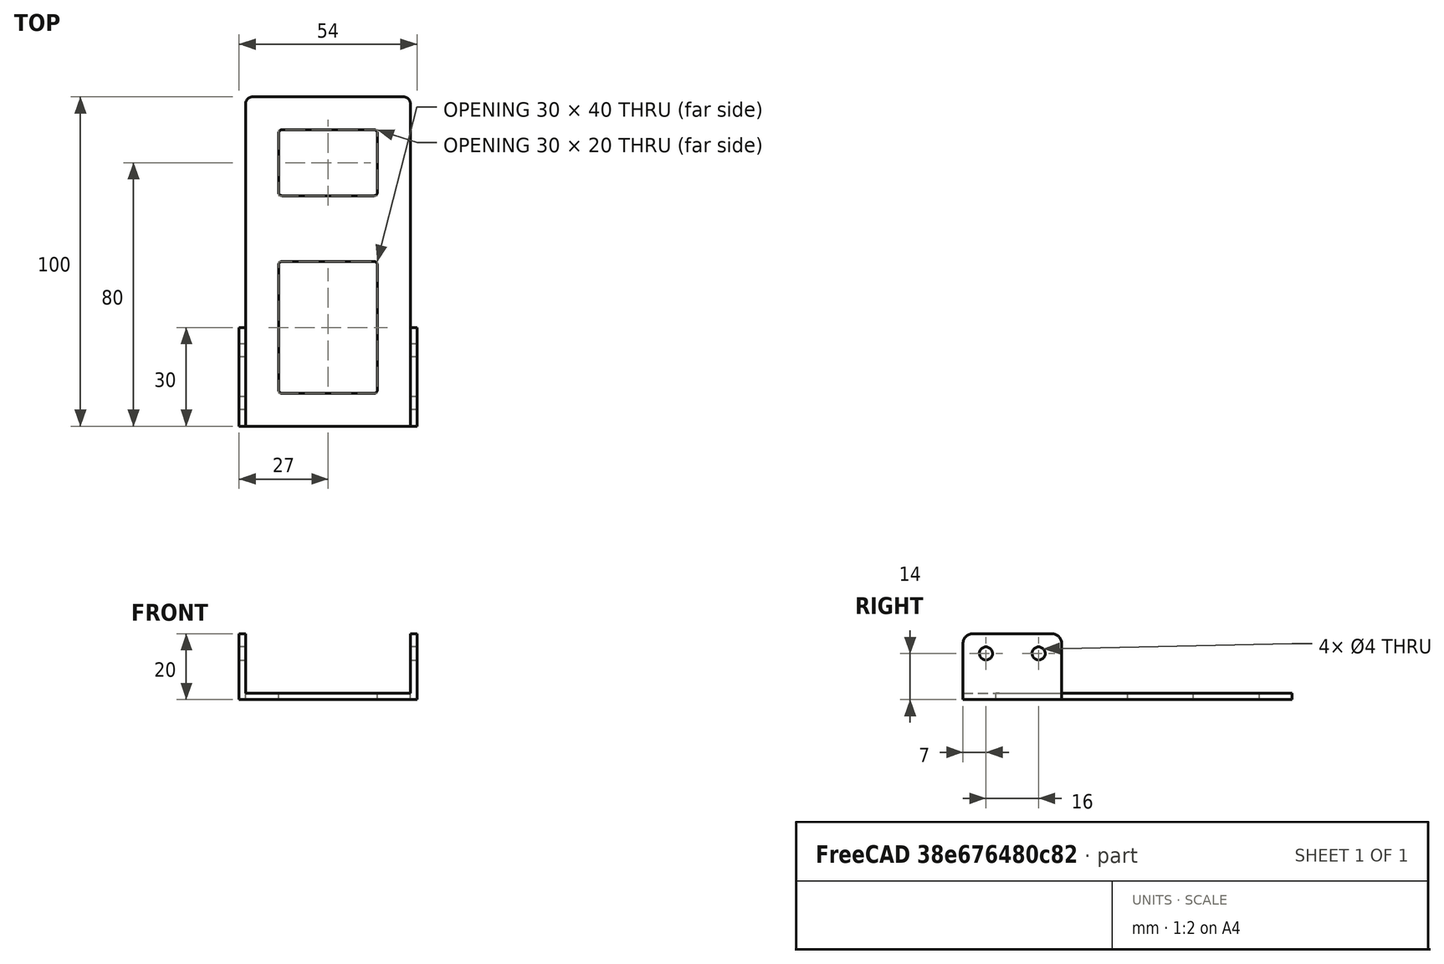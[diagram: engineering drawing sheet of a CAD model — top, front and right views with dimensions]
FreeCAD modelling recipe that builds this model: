
FCSTD DOCUMENT  (FreeCAD 1.0R39319 (Git))
Label: ojt1_t12r03_universal_suport
License: All rights reserved
LicenseURL: https://en.wikipedia.org/wiki/All_rights_reserved
objects: Part::Fillet×6, Part::Cut×6, Part::Box×5, Part::Cylinder×4, Part::MultiFuse×1
note: 22 computed .brp shape members not serialized (recipe doc carries the construction recipe); baked Part::Feature solids carry a one-line shape summary decoded from their .brp

FEATURE [Part::Box] Box  label="Cube"
  AttacherType = Attacher::AttachEngine3D
  Height = 2
  Length = 50
  Width = 100
FEATURE [Part::Fillet] Fillet
  Base = -> Box
  EdgeLinks = -> Box [Edge7]
  Edges = 1 edges r=2: [Edge7]
FEATURE [Part::Fillet] Fillet001
  Base = -> Fillet
  EdgeLinks = -> Fillet [Edge15]
  Edges = 1 edges r=2: [Edge15]
FEATURE [Part::Box] Box001  label="Cube001"
  AttacherType = Attacher::AttachEngine3D
  Height = 10
  Length = 30
  Placement = pos=(10,70,0) rot=(0,0,1;0rad)
  Width = 20
FEATURE [Part::Fillet] Fillet002
  Base = -> Box001
  EdgeLinks = -> Box001 [Edge1,Edge3,Edge5,Edge7]
  Edges = 4 edges r=1: [Edge1,Edge3,Edge5,Edge7]
FEATURE [Part::Cut] Cut
  Base = -> Fillet001
  Refine = true
  Tool = -> Fillet002
FEATURE [Part::Box] Box002  label="Cube002"
  AttacherType = Attacher::AttachEngine3D
  Height = 10
  Length = 30
  Placement = pos=(10,10,0) rot=(0,0,1;0rad)
  Width = 40
FEATURE [Part::Fillet] Fillet003
  Base = -> Box002
  EdgeLinks = -> Box002 [Edge1,Edge3,Edge5,Edge7]
  Edges = 4 edges r=1: [Edge1,Edge3,Edge5,Edge7]
FEATURE [Part::Cut] Cut001
  Base = -> Cut
  Refine = true
  Tool = -> Fillet003
FEATURE [Part::Box] Box003  label="Cube003"
  AttacherType = Attacher::AttachEngine3D
  Height = 20
  Length = 2
  Placement = pos=(-2,0,0) rot=(0,0,1;0rad)
  Width = 30
FEATURE [Part::Fillet] Fillet004
  Base = -> Box003
  EdgeLinks = -> Box003 [Edge10,Edge12]
  Edges = 2 edges r=3: [Edge10,Edge12]
FEATURE [Part::Cylinder] Cylinder
  Angle = 360
  AttacherType = Attacher::AttachEngine3D
  FirstAngle = 0
  Height = 10
  Placement = pos=(-6,7,14) rot=(10,1000000000,0;1.5708rad)
  Radius = 2
  SecondAngle = 0
FEATURE [Part::Cylinder] Cylinder001
  Angle = 360
  AttacherType = Attacher::AttachEngine3D
  FirstAngle = 0
  Height = 10
  Placement = pos=(-6,23,14) rot=(10,1000000000,0;1.5708rad)
  Radius = 2
  SecondAngle = 0
FEATURE [Part::Cut] Cut002
  Base = -> Fillet004
  Refine = true
  Tool = -> Cylinder
FEATURE [Part::Cut] Cut003
  Base = -> Cut002
  Refine = true
  Tool = -> Cylinder001
FEATURE [Part::Box] Box004  label="Cube004"
  AttacherType = Attacher::AttachEngine3D
  Height = 20
  Length = 2
  Placement = pos=(-2,0,0) rot=(0,0,1;0rad)
  Width = 30
FEATURE [Part::Cylinder] Cylinder002
  Angle = 360
  AttacherType = Attacher::AttachEngine3D
  FirstAngle = 0
  Height = 10
  Placement = pos=(-6,7,14) rot=(10,1000000000,0;1.5708rad)
  Radius = 2
  SecondAngle = 0
FEATURE [Part::Cylinder] Cylinder003
  Angle = 360
  AttacherType = Attacher::AttachEngine3D
  FirstAngle = 0
  Height = 10
  Placement = pos=(-6,23,14) rot=(10,1000000000,0;1.5708rad)
  Radius = 2
  SecondAngle = 0
FEATURE [Part::Fillet] Fillet005
  Base = -> Box004
  EdgeLinks = -> Box004 [Edge10,Edge12]
  Edges = 2 edges r=3: [Edge10,Edge12]
FEATURE [Part::Cut] Cut004
  Base = -> Fillet005
  Refine = true
  Tool = -> Cylinder002
FEATURE [Part::Cut] Cut005
  Base = -> Cut004
  Placement = pos=(52,0,0) rot=(0,0,1;0rad)
  Refine = true
  Tool = -> Cylinder003
FEATURE [Part::MultiFuse] Fusion
  Refine = true
  Shapes = -> [Cut001,Cut003,Cut005]
